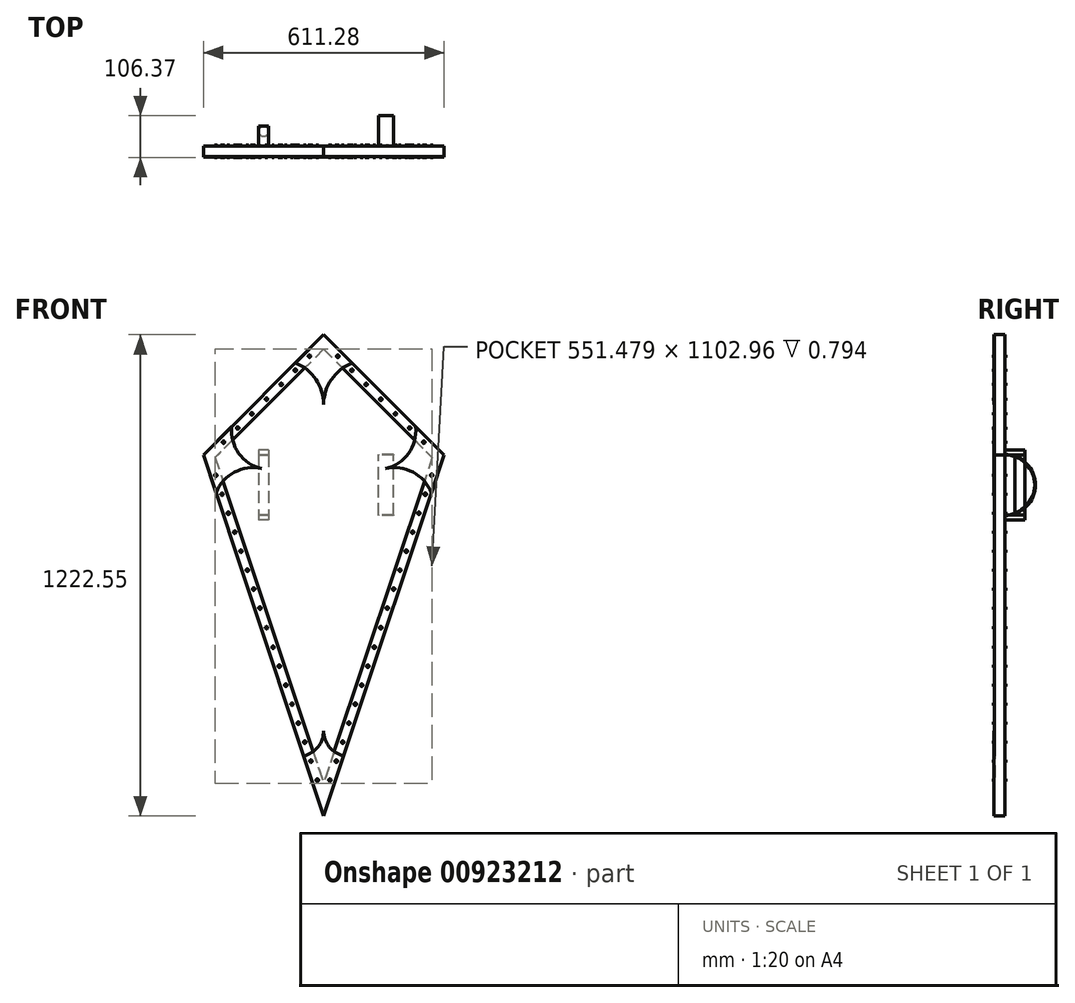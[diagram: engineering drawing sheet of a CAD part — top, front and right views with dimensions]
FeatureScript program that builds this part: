
annotation { "Feature Type Name" : "Feature", "Feature Type Description" : "" }
export const myFeature = defineFeature(function(context is Context, id is Id, definition is map)
    precondition{}
    {
        {
            var Q0;
            Q0=qCreatedBy(makeId("Front.planeOp"),FACE);
            var sketch = newSketch(context, id + "F0", { "sketchPlane" : qUnion([Q0])});
            skLineSegment(sketch, "E0", {"start": v(0, 0) * mm, "end": v(0, 1219.2) * mm, "construction": true});
            skPoint(sketch, "E1", {"position": v(0, 914.4) * mm});
            skLineSegment(sketch, "E2", {"start": v(0, 0) * mm, "end": v(304.8, 914.4) * mm});
            skLineSegment(sketch, "E3", {"start": v(304.8, 914.4) * mm, "end": v(0, 1219.2) * mm});
            skLineSegment(sketch, "E4.MirrorCS", {"start": v(-304.8, 914.4) * mm, "end": v(0, 1219.2) * mm});
            skLineSegment(sketch, "E5.MirrorCS", {"start": v(0, 0) * mm, "end": v(-304.8, 914.4) * mm});
            skLineSegment(sketch, "E6", {"start": v(0, -2.51) * mm, "end": v(305.64, 914.4) * mm});
            skLineSegment(sketch, "E7", {"start": v(305.64, 914.4) * mm, "end": v(0, 1220.04) * mm});
            skLineSegment(sketch, "E8", {"start": v(0, 1220.04) * mm, "end": v(-305.64, 914.4) * mm});
            skLineSegment(sketch, "E9", {"start": v(-305.64, 914.4) * mm, "end": v(0, -2.51) * mm});
            skSolve(sketch);
        }
        {
            var Q0;
            Q0 = qSketchRegion(id + "F0", true);
            extrude(context, id + "F1", {"entities" : qUnion([Q0]), "depth" : 25.4 * mm, "offsetDistance" : 25.4 * mm});
        }
        {
            var Q0;
            Q0=makeQuery(id+"F0.imprint","IMPRINT",FACE,{"disambiguationData":[TD([[makeQuery(id+"F0.imprint","IMPRINT",EDGE,{"derivedFrom":sQuery(id+"F0.wireOp",EDGE,"E2")}),1.0]])]});
            extrude(context, id + "F2", {"entities" : qUnion([Q0]), "depth" : 25.4 * mm, "offsetDistance" : 25.4 * mm});
        }
        {
            var Q0;
            Q0=qCreatedBy(makeId("Front.planeOp"),FACE);
            var sketch = newSketch(context, id + "F3", { "sketchPlane" : qUnion([Q0])});
            skLineSegment(sketch, "E10", {"start": v(0, 0) * mm, "end": v(0, 1219.2) * mm, "construction": true});
            skPoint(sketch, "E11", {"position": v(0, 914.4) * mm});
            skLineSegment(sketch, "E12", {"start": v(0, 1219.2) * mm, "end": v(304.8, 914.4) * mm, "construction": true});
            skLineSegment(sketch, "E13", {"start": v(304.8, 914.4) * mm, "end": v(0, 0) * mm, "construction": true});
            skLineSegment(sketch, "E14", {"start": v(0, 1183.28) * mm, "end": v(275.74, 907.54) * mm});
            skLineSegment(sketch, "E15", {"start": v(275.74, 907.54) * mm, "end": v(0, 80.32) * mm});
            skLineSegment(sketch, "E16.MirrorCS", {"start": v(0, 1183.28) * mm, "end": v(-275.74, 907.54) * mm});
            skLineSegment(sketch, "E17.MirrorCS", {"start": v(0, 1219.2) * mm, "end": v(-304.8, 914.4) * mm, "construction": true});
            skLineSegment(sketch, "E18.MirrorCS", {"start": v(-304.8, 914.4) * mm, "end": v(0, 0) * mm, "construction": true});
            skLineSegment(sketch, "E19.MirrorCS", {"start": v(-275.74, 907.54) * mm, "end": v(0, 80.32) * mm});
            skLineSegment(sketch, "E20", {"start": v(0, 1220.04) * mm, "end": v(305.64, 914.4) * mm});
            skLineSegment(sketch, "E21", {"start": v(305.64, 914.4) * mm, "end": v(0, -2.51) * mm});
            skLineSegment(sketch, "E22", {"start": v(0, -2.51) * mm, "end": v(-305.64, 914.4) * mm});
            skLineSegment(sketch, "E23", {"start": v(-305.64, 914.4) * mm, "end": v(0, 1220.04) * mm});
            skSolve(sketch);
        }
        {
            var Q0;
            Q0=makeQuery(id+"F3.imprint","IMPRINT",FACE,{"disambiguationData":[TD([[makeQuery(id+"F3.imprint","IMPRINT",EDGE,{"derivedFrom":sQuery(id+"F3.wireOp",EDGE,"E14")}),1.0]])]});
            extrude(context, id + "F4", {"entities" : qUnion([Q0]), "operationType" : NewBodyOperationType.ADD, "depth" : 26.2 * mm, "offsetDistance" : 25.4 * mm, "hasSecondDirection" : true, "secondDirectionOppositeDirection" : false, "secondDirectionDepth" : 25.4 * mm});
        }
        {
            var Q0;
            Q0=makeQuery(id+"F3.imprint","IMPRINT",FACE,{"disambiguationData":[TD([[makeQuery(id+"F3.imprint","IMPRINT",EDGE,{"derivedFrom":sQuery(id+"F3.wireOp",EDGE,"E14")}),1.0]])]});
            extrude(context, id + "F5", {"entities" : qUnion([Q0]), "operationType" : NewBodyOperationType.ADD, "oppositeDirection" : true, "depth" : 0.8 * mm, "offsetDistance" : 25.4 * mm});
        }
        {
            var Q0;
            Q0=qCreatedBy(makeId("Front.planeOp"),FACE);
            var sketch = newSketch(context, id + "F6", { "sketchPlane" : qUnion([Q0])});
            skLineSegment(sketch, "E24", {"start": v(0, -2.51) * mm, "end": v(0, 213.39) * mm, "construction": true});
            skLineSegment(sketch, "E25", {"start": v(0, -2.51) * mm, "end": v(50.8, 149.89) * mm});
            skArc(sketch, "E26", {"start": v(0, 213.39) * mm, "mid": v(14.26, 172.73) * mm, "end": v(50.8, 149.89) * mm});
            skArc(sketch, "E27.MirrorCS", {"start": v(0, 213.39) * mm, "mid": v(-14.26, 172.73) * mm, "end": v(-50.8, 149.89) * mm});
            skLineSegment(sketch, "E28.MirrorCS", {"start": v(0, -2.51) * mm, "end": v(-50.8, 149.89) * mm});
            skPoint(sketch, "E29", {"position": v(305.6, 914.4) * mm});
            skLineSegment(sketch, "E30", {"start": v(305.6, 914.4) * mm, "end": v(273.47, 818.01) * mm});
            skLineSegment(sketch, "E31", {"start": v(305.6, 914.4) * mm, "end": v(233.75, 986.24) * mm});
            skLineSegment(sketch, "E32", {"start": v(233.75, 986.24) * mm, "end": v(273.47, 818.01) * mm, "construction": true});
            skLineSegment(sketch, "E33", {"start": v(305.6, 914.4) * mm, "end": v(157.27, 879.39) * mm, "construction": true});
            skArc(sketch, "E34", {"start": v(273.47, 818.01) * mm, "mid": v(226.88, 870.5) * mm, "end": v(157.27, 879.39) * mm});
            skArc(sketch, "E35", {"start": v(157.27, 879.39) * mm, "mid": v(215.55, 918.47) * mm, "end": v(233.75, 986.24) * mm});
            skArc(sketch, "E36.MirrorCS", {"start": v(-157.27, 879.39) * mm, "mid": v(-215.55, 918.47) * mm, "end": v(-233.75, 986.24) * mm});
            skLineSegment(sketch, "E37.MirrorCS", {"start": v(-305.6, 914.4) * mm, "end": v(-233.75, 986.24) * mm});
            skArc(sketch, "E38.MirrorCS", {"start": v(-273.47, 818.01) * mm, "mid": v(-226.88, 870.5) * mm, "end": v(-157.27, 879.39) * mm});
            skLineSegment(sketch, "E39.MirrorCS", {"start": v(-305.6, 914.4) * mm, "end": v(-273.47, 818.01) * mm});
            skLineSegment(sketch, "E40", {"start": v(0, 1220) * mm, "end": v(0, 1042.2) * mm, "construction": true});
            skLineSegment(sketch, "E41", {"start": v(0, 1220) * mm, "end": v(71.84, 1148.15) * mm});
            skLineSegment(sketch, "E42", {"start": v(0, 1220) * mm, "end": v(-71.84, 1148.15) * mm});
            skArc(sketch, "E43", {"start": v(71.84, 1148.15) * mm, "mid": v(19.65, 1106.2) * mm, "end": v(0, 1042.2) * mm});
            skArc(sketch, "E44", {"start": v(0, 1042.2) * mm, "mid": v(-19.65, 1106.2) * mm, "end": v(-71.84, 1148.15) * mm});
            skSolve(sketch);
        }
        {
            var Q0;
            Q0 = qSketchRegion(id + "F6", true);
            extrude(context, id + "F7", {"entities" : qUnion([Q0]), "depth" : 26.99 * mm, "offsetDistance" : 25.4 * mm, "hasSecondDirection" : true, "secondDirectionOppositeDirection" : false, "secondDirectionDepth" : 26.2 * mm});
        }
        {
            var Q0;
            Q0=qCreatedBy(makeId("Front.planeOp"),FACE);
            var sketch = newSketch(context, id + "F8", { "sketchPlane" : qUnion([Q0])});
            skLineSegment(sketch, "E45", {"start": v(0, 0) * mm, "end": v(0, 1219.2) * mm, "construction": true});
            skLineSegment(sketch, "E46", {"start": v(0, 1219.2) * mm, "end": v(304.8, 914.4) * mm, "construction": true});
            skLineSegment(sketch, "E47", {"start": v(304.8, 914.4) * mm, "end": v(0, 0) * mm, "construction": true});
            skLineSegment(sketch, "E48", {"start": v(0, 1201.24) * mm, "end": v(290.27, 910.97) * mm, "construction": true});
            skLineSegment(sketch, "E49", {"start": v(290.27, 910.97) * mm, "end": v(0, 40.16) * mm, "construction": true});
            skCircle(sketch, "E50", {"center": v(16.06, 88.35) * mm, "radius": 3.17 * mm});
            skCircle(sketch, "E51", {"center": v(32.13, 136.55) * mm, "radius": 3.18 * mm});
            skPoint(sketch, "E52", {"position": v(145.13, 475.57) * mm});
            skLineSegment(sketch, "E53", {"start": v(145.13, 475.57) * mm, "end": v(96.94, 491.63) * mm, "construction": true});
            skCircle(sketch, "E54", {"center": v(48.2, 184.74) * mm, "radius": 3.18 * mm});
            skCircle(sketch, "E55", {"center": v(64.26, 232.93) * mm, "radius": 3.18 * mm});
            skCircle(sketch, "E56", {"center": v(80.32, 281.13) * mm, "radius": 3.18 * mm});
            skCircle(sketch, "E57", {"center": v(96.39, 329.32) * mm, "radius": 3.18 * mm});
            skCircle(sketch, "E58", {"center": v(112.45, 377.51) * mm, "radius": 3.18 * mm});
            skCircle(sketch, "E59", {"center": v(128.51, 425.7) * mm, "radius": 3.18 * mm});
            skCircle(sketch, "E60.MirrorC", {"center": v(161.75, 525.42) * mm, "radius": 3.18 * mm});
            skCircle(sketch, "E61.MirrorC", {"center": v(177.82, 573.62) * mm, "radius": 3.18 * mm});
            skCircle(sketch, "E62.MirrorC", {"center": v(193.88, 621.81) * mm, "radius": 3.18 * mm});
            skCircle(sketch, "E63.MirrorC", {"center": v(209.95, 670) * mm, "radius": 3.18 * mm});
            skCircle(sketch, "E64.MirrorC", {"center": v(226.01, 718.2) * mm, "radius": 3.18 * mm});
            skCircle(sketch, "E65.MirrorC", {"center": v(242.08, 766.4) * mm, "radius": 3.18 * mm});
            skCircle(sketch, "E66.MirrorC", {"center": v(258.14, 814.58) * mm, "radius": 3.18 * mm});
            skCircle(sketch, "E67.MirrorC", {"center": v(274.2, 862.78) * mm, "radius": 3.17 * mm});
            skPoint(sketch, "E68", {"position": v(145.13, 1056.1) * mm});
            skLineSegment(sketch, "E69", {"start": v(145.13, 1056.1) * mm, "end": v(109.21, 1020.18) * mm, "construction": true});
            skCircle(sketch, "E70", {"center": v(254.35, 946.9) * mm, "radius": 3.18 * mm});
            skCircle(sketch, "E71", {"center": v(218.43, 982.81) * mm, "radius": 3.18 * mm});
            skCircle(sketch, "E72", {"center": v(182.5, 1018.73) * mm, "radius": 3.18 * mm});
            skCircle(sketch, "E73.MirrorC", {"center": v(107.76, 1093.48) * mm, "radius": 3.18 * mm});
            skCircle(sketch, "E74.MirrorC", {"center": v(71.84, 1129.4) * mm, "radius": 3.18 * mm});
            skCircle(sketch, "E75.MirrorC", {"center": v(35.92, 1165.32) * mm, "radius": 3.18 * mm});
            skCircle(sketch, "E76.MirrorC", {"center": v(-35.92, 1165.32) * mm, "radius": 3.18 * mm});
            skCircle(sketch, "E77.MirrorC", {"center": v(-71.84, 1129.4) * mm, "radius": 3.18 * mm});
            skCircle(sketch, "E78.MirrorC", {"center": v(-107.76, 1093.48) * mm, "radius": 3.18 * mm});
            skCircle(sketch, "E79.MirrorC", {"center": v(-182.5, 1018.73) * mm, "radius": 3.18 * mm});
            skCircle(sketch, "E80.MirrorC", {"center": v(-218.43, 982.81) * mm, "radius": 3.18 * mm});
            skCircle(sketch, "E81.MirrorC", {"center": v(-254.35, 946.9) * mm, "radius": 3.18 * mm});
            skCircle(sketch, "E82.MirrorC", {"center": v(-274.2, 862.78) * mm, "radius": 3.17 * mm});
            skPoint(sketch, "E83.MirrorP", {"position": v(-145.13, 1056.1) * mm});
            skCircle(sketch, "E84.MirrorC", {"center": v(-258.14, 814.58) * mm, "radius": 3.18 * mm});
            skCircle(sketch, "E85.MirrorC", {"center": v(-242.08, 766.4) * mm, "radius": 3.18 * mm});
            skCircle(sketch, "E86.MirrorC", {"center": v(-226.01, 718.2) * mm, "radius": 3.18 * mm});
            skCircle(sketch, "E87.MirrorC", {"center": v(-209.95, 670) * mm, "radius": 3.18 * mm});
            skCircle(sketch, "E88.MirrorC", {"center": v(-193.88, 621.81) * mm, "radius": 3.18 * mm});
            skCircle(sketch, "E89.MirrorC", {"center": v(-177.82, 573.62) * mm, "radius": 3.18 * mm});
            skCircle(sketch, "E90.MirrorC", {"center": v(-161.75, 525.42) * mm, "radius": 3.18 * mm});
            skCircle(sketch, "E91.MirrorC", {"center": v(-128.51, 425.7) * mm, "radius": 3.18 * mm});
            skCircle(sketch, "E92.MirrorC", {"center": v(-112.45, 377.51) * mm, "radius": 3.18 * mm});
            skCircle(sketch, "E93.MirrorC", {"center": v(-96.39, 329.32) * mm, "radius": 3.18 * mm});
            skCircle(sketch, "E94.MirrorC", {"center": v(-80.32, 281.13) * mm, "radius": 3.18 * mm});
            skCircle(sketch, "E95.MirrorC", {"center": v(-64.26, 232.93) * mm, "radius": 3.18 * mm});
            skCircle(sketch, "E96.MirrorC", {"center": v(-48.2, 184.74) * mm, "radius": 3.18 * mm});
            skCircle(sketch, "E97.MirrorC", {"center": v(-32.13, 136.55) * mm, "radius": 3.18 * mm});
            skCircle(sketch, "E98", {"center": v(145.13, 475.57) * mm, "radius": 3.18 * mm});
            skCircle(sketch, "E99", {"center": v(145.13, 1056.1) * mm, "radius": 3.18 * mm});
            skCircle(sketch, "E100.MirrorC", {"center": v(-145.13, 1056.1) * mm, "radius": 3.18 * mm});
            skCircle(sketch, "E101.MirrorC", {"center": v(-145.13, 475.57) * mm, "radius": 3.18 * mm});
            skCircle(sketch, "E102.MirrorC", {"center": v(-16.06, 88.35) * mm, "radius": 3.17 * mm});
            skSolve(sketch);
        }
        {
            var Q0;
            Q0 = qSketchRegion(id + "F8", true);
            extrude(context, id + "F9", {"entities" : qUnion([Q0]), "operationType" : NewBodyOperationType.ADD, "depth" : 28.57 * mm, "offsetDistance" : 25.4 * mm, "hasSecondDirection" : true, "secondDirectionOppositeDirection" : true, "secondDirectionDepth" : 3.17 * mm});
        }
        {
            var Q0;
            Q0=qCreatedBy(makeId("Top.planeOp"),FACE);
            var sketch = newSketch(context, id + "F10", { "sketchPlane" : qUnion([Q0])});
            skCircle(sketch, "E103", {"center": v(-152.4, 38.1) * mm, "radius": 12.7 * mm});
            skSolve(sketch);
        }
        {
            var Q0;
            Q0 = qSketchRegion(id + "F10", true);
            extrude(context, id + "F11", {"entities" : qUnion([Q0]), "depth" : 914.4 * mm, "offsetDistance" : 25.4 * mm, "hasSecondDirection" : true, "secondDirectionOppositeDirection" : false, "secondDirectionDepth" : 762 * mm});
        }
        {
            var Q0;
            Q0=qCreatedBy(makeId("Front.planeOp"),FACE);
            var sketch = newSketch(context, id + "F12", { "sketchPlane" : qUnion([Q0])});
            skLineSegment(sketch, "E104.bottom", {"start": v(-139.7, 927.1) * mm, "end": v(-165.1, 927.1) * mm});
            skLineSegment(sketch, "E104.top", {"start": v(-139.7, 914.4) * mm, "end": v(-165.1, 914.4) * mm});
            skLineSegment(sketch, "E104.left", {"start": v(-139.7, 927.1) * mm, "end": v(-139.7, 914.4) * mm});
            skLineSegment(sketch, "E104.right", {"start": v(-165.1, 927.1) * mm, "end": v(-165.1, 914.4) * mm});
            skLineSegment(sketch, "E105.bottom", {"start": v(-139.7, 762) * mm, "end": v(-165.1, 762) * mm});
            skLineSegment(sketch, "E105.top", {"start": v(-139.7, 749.3) * mm, "end": v(-165.1, 749.3) * mm});
            skLineSegment(sketch, "E105.left", {"start": v(-139.7, 762) * mm, "end": v(-139.7, 749.3) * mm});
            skLineSegment(sketch, "E105.right", {"start": v(-165.1, 762) * mm, "end": v(-165.1, 749.3) * mm});
            skSolve(sketch);
        }
        {
            var Q0;
            Q0 = qSketchRegion(id + "F12", true);
            extrude(context, id + "F13", {"entities" : qUnion([Q0]), "operationType" : NewBodyOperationType.ADD, "oppositeDirection" : true, "depth" : 50.8 * mm, "offsetDistance" : 25.4 * mm});
        }
        {
            var Q0;
            Q0=qCreatedBy(makeId("Right.planeOp"),FACE);
            var sketch = newSketch(context, id + "F14", { "sketchPlane" : qUnion([Q0])});
            skArc(sketch, "E106", {"start": v(0, 914.4) * mm, "mid": v(76.2, 838.2) * mm, "end": v(0, 762) * mm});
            skArc(sketch, "E107", {"start": v(0, 760.41) * mm, "mid": v(77.79, 838.2) * mm, "end": v(0, 915.99) * mm});
            skLineSegment(sketch, "E108", {"start": v(0, 915.99) * mm, "end": v(0, 914.4) * mm});
            skLineSegment(sketch, "E109", {"start": v(0, 762) * mm, "end": v(0, 760.41) * mm});
            skSolve(sketch);
        }
        {
            var Q0;
            Q0 = qSketchRegion(id + "F14", true);
            extrude(context, id + "F15", {"entities" : qUnion([Q0]), "operationType" : NewBodyOperationType.ADD, "depth" : 177.8 * mm, "offsetDistance" : 25.4 * mm, "hasSecondDirection" : true, "secondDirectionOppositeDirection" : false, "secondDirectionDepth" : 139.7 * mm});
        }
    });
